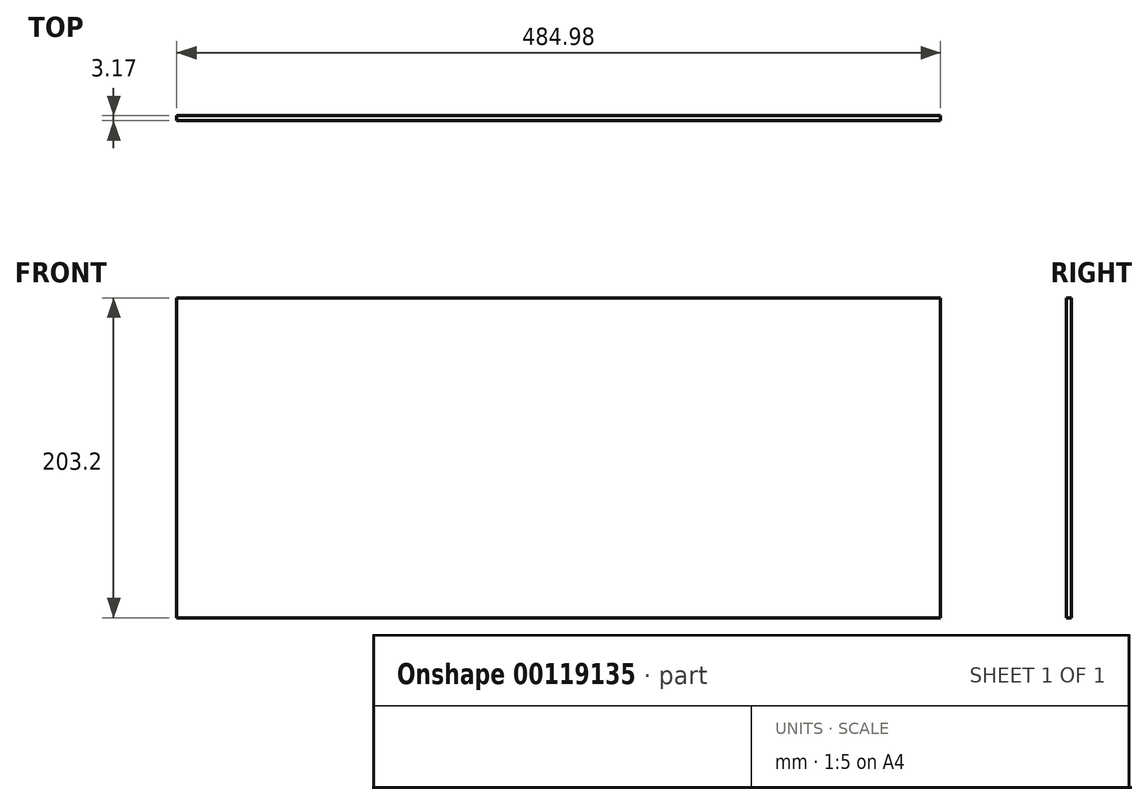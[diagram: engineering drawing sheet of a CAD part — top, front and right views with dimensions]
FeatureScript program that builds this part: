
annotation { "Feature Type Name" : "Feature", "Feature Type Description" : "" }
export const myFeature = defineFeature(function(context is Context, id is Id, definition is map)
    precondition{}
    {
        {
            var Q0;
            Q0=qCreatedBy(makeId("Front.planeOp"),FACE);
            var sketch = newSketch(context, id + "F0", { "sketchPlane" : qUnion([Q0])});
            skLineSegment(sketch, "E0.bottom", {"start": v(-242.5, 101.6) * mm, "end": v(242.5, 101.6) * mm});
            skLineSegment(sketch, "E0.top", {"start": v(-242.5, -101.6) * mm, "end": v(242.5, -101.6) * mm});
            skLineSegment(sketch, "E0.left", {"start": v(-242.5, 101.6) * mm, "end": v(-242.5, -101.6) * mm});
            skLineSegment(sketch, "E0.right", {"start": v(242.5, 101.6) * mm, "end": v(242.5, -101.6) * mm});
            skLineSegment(sketch, "E1", {"start": v(-242.5, -101.6) * mm, "end": v(242.5, 101.6) * mm, "construction": true});
            skSolve(sketch);
        }
        {
            var Q0;
            Q0=makeQuery(id+"F0.imprint","IMPRINT",FACE,{"disambiguationData":[TD([[makeQuery(id+"F0.imprint","IMPRINT",EDGE,{"derivedFrom":sQuery(id+"F0.wireOp",EDGE,"E0.bottom")}),-1.0]])]});
            var Q1;
            Q1=sQuery(id+"F0.wireOp",EDGE,"E1");
            extrude(context, id + "F1", {"entities" : qUnion([Q0]), "surfaceEntities" : qUnion([Q1]), "depth" : 3.17 * mm});
        }
    });
